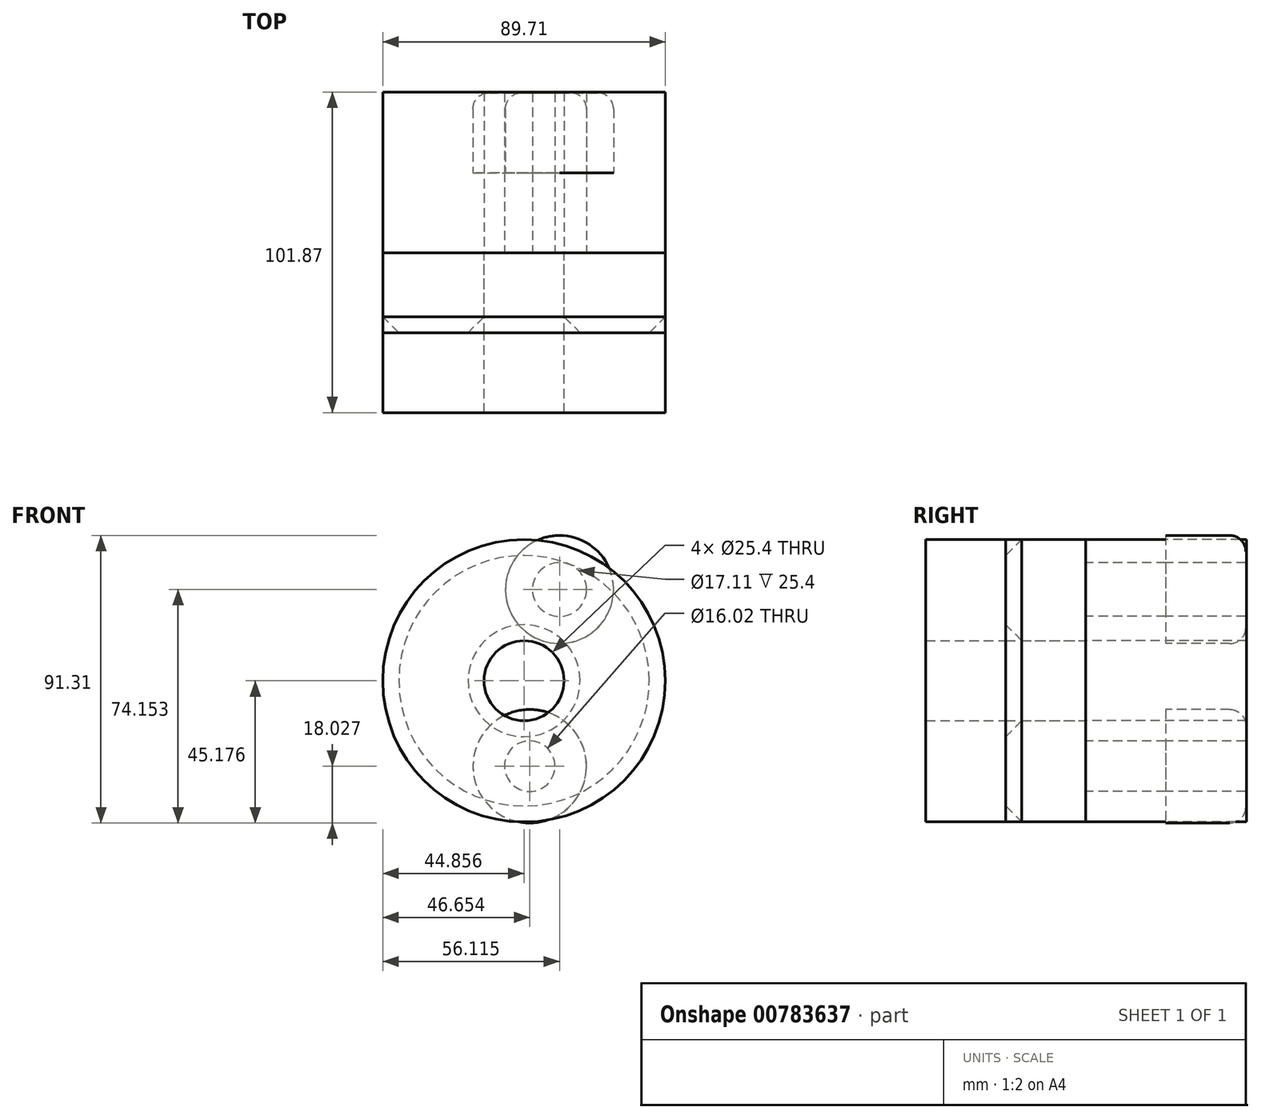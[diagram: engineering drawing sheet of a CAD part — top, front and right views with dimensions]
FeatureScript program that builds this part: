
annotation { "Feature Type Name" : "Feature", "Feature Type Description" : "" }
export const myFeature = defineFeature(function(context is Context, id is Id, definition is map)
    precondition{}
    {
        {
            var Q0;
            Q0=qCreatedBy(makeId("Front.planeOp"),FACE);
            var sketch = newSketch(context, id + "F0", { "sketchPlane" : qUnion([Q0])});
            skCircle(sketch, "E0", {"center": v(-24.07, 18.9) * mm, "radius": 44.86 * mm});
            skSolve(sketch);
        }
        {
            var Q0;
            Q0=makeQuery(id+"F0.imprint","IMPRINT",FACE,{"disambiguationData":[TD([[makeQuery(id+"F0.imprint","IMPRINT",EDGE,{"derivedFrom":sQuery(id+"F0.wireOp",EDGE,"E0")}),1.0]])]});
            var sketch = newSketch(context, id + "F1", { "sketchPlane" : qUnion([Q0])});
            skLineSegment(sketch, "E1.bottom", {"start": v(-31.53, 27.59) * mm, "end": v(-13.5, 27.59) * mm});
            skLineSegment(sketch, "E1.top", {"start": v(-31.53, 11.47) * mm, "end": v(-13.5, 11.47) * mm});
            skLineSegment(sketch, "E1.left", {"start": v(-31.53, 27.59) * mm, "end": v(-31.53, 11.47) * mm});
            skLineSegment(sketch, "E1.right", {"start": v(-13.5, 27.59) * mm, "end": v(-13.5, 11.47) * mm});
            skPoint(sketch, "E1.middle", {"position": v(-22.52, 19.53) * mm});
            skSolve(sketch);
        }
        {
            var Q0;
            Q0=makeQuery(id+"F1.imprint","IMPRINT",FACE,{"disambiguationData":[TD([[makeQuery(id+"F1.imprint","IMPRINT",EDGE,{"derivedFrom":sQuery(id+"F1.wireOp",EDGE,"E1.bottom")}),1.0]])]});
            var Q1;
            Q1=makeQuery(id+"F0.imprint","IMPRINT",FACE,{"disambiguationData":[TD([[makeQuery(id+"F0.imprint","IMPRINT",EDGE,{"derivedFrom":sQuery(id+"F0.wireOp",EDGE,"E0")}),1.0]])]});
            var Q2;
            Q2 = qSketchRegion(id + "F1", true);
            extrude(context, id + "F2", {"entities" : qUnion([Q0, Q1, Q2]), "depth" : 25.4 * mm, "offsetDistance" : 25.4 * mm});
        }
        {
            var Q0;
            {var subQ0=sQuery(id+"F0.wireOp",EDGE,"E0");Q0=makeQuery(id+"F2.opExtrude","CAP_FACE",FACE,{"disambiguationData":[OSD([subQ0]),TDD([makeQuery(id+"F0.imprint","IMPRINT",EDGE,{"derivedFrom":subQ0})])],"isStart":false});}
            var sketch = newSketch(context, id + "F3", { "sketchPlane" : qUnion([Q0])});
            skPoint(sketch, "E2", {"position": v(-24.07, 18.9) * mm});
            skSolve(sketch);
        }
        {
            var Q0;
            {var subQ0=sQuery(id+"F0.wireOp",EDGE,"E0");Q0=makeQuery(id+"F2.opExtrude","CAP_FACE",FACE,{"disambiguationData":[OSD([subQ0]),TDD([makeQuery(id+"F0.imprint","IMPRINT",EDGE,{"derivedFrom":subQ0})])],"isStart":true});}
            var sketch = newSketch(context, id + "F4", { "sketchPlane" : qUnion([Q0])});
            skPoint(sketch, "E3", {"position": v(24.07, 18.9) * mm});
            skSolve(sketch);
        }
        {
            var Q0;
            Q0=sQuery(id+"F4.wireOp",VERTEX,"E3");
            var Q1;
            Q1=sQuery(id+"F3.wireOp",VERTEX,"E2");
            var Q2;
            {var subQ0=sQuery(id+"F0.wireOp",EDGE,"E0");Q2=makeQuery(id+"F2.opExtrude","SWEPT_BODY",BODY,{"disambiguationData":[OSD([subQ0]),TDD([makeQuery(id+"F0.imprint","IMPRINT",EDGE,{"derivedFrom":subQ0})])]});}
            var Q3;
            {var subQ0=sQuery(id+"F0.wireOp",EDGE,"E0");Q3=makeQuery(id+"F2.opExtrude","SWEPT_BODY",BODY,{"disambiguationData":[OSD([subQ0]),TDD([makeQuery(id+"F1.imprint","IMPRINT",EDGE,{"derivedFrom":makeQuery(id+"F0.imprint","IMPRINT",EDGE,{"derivedFrom":subQ0})})])]});}
            hole(context, id + "F5", {"style" : HoleStyle.SIMPLE, "endStyle" : HoleEndStyle.THROUGH, "holeDiameter" : 25.4 * mm, "majorDiameter" : 6.35 * mm, "isTappedThrough" : true, "tappedDepth" : 12.7 * mm, "tapClearance" : 3, "locations" : qUnion([Q0, Q1]), "scope" : qUnion([Q2, Q3])});
        }
        {
            var Q0;
            {var subQ0=sQuery(id+"F0.wireOp",EDGE,"E0");Q0=makeQuery(id+"F2.opExtrude","CAP_FACE",FACE,{"disambiguationData":[OSD([subQ0]),TDD([makeQuery(id+"F1.imprint","IMPRINT",EDGE,{"derivedFrom":makeQuery(id+"F0.imprint","IMPRINT",EDGE,{"derivedFrom":subQ0})})])],"isStart":false});}
            chamfer(context, id + "F6", {"entities" : qUnion([Q0]), "width" : 5.08 * mm, "tangentPropagation" : true});
        }
        {
            var Q0;
            {var subQ0=sQuery(id+"F0.wireOp",EDGE,"E0");Q0=makeQuery(id+"F2.opExtrude","CAP_FACE",FACE,{"disambiguationData":[OSD([subQ0]),TDD([makeQuery(id+"F0.imprint","IMPRINT",EDGE,{"derivedFrom":subQ0})])],"isStart":false});}
            var sketch = newSketch(context, id + "F7", { "sketchPlane" : qUnion([Q0])});
            skSolve(sketch);
        }
        {
            var Q0;
            {var subQ0=sQuery(id+"F0.wireOp",EDGE,"E0");var subQ1=makeQuery(id+"F0.imprint","IMPRINT",EDGE,{"derivedFrom":subQ0});Q0=makeQuery(id+"F7.imprint","IMPRINT",FACE,{"disambiguationData":[TD([[makeQuery(id+"F7.imprint","IMPRINT",EDGE,{"derivedFrom":makeQuery(id+"F2.opExtrude","CAP_EDGE",EDGE,{"disambiguationData":[OSD([subQ0]),TDD([subQ1])],"isStart":false})}),1.0]])]});}
            extrude(context, id + "F8", {"entities" : qUnion([Q0]), "depth" : 25.4 * mm, "offsetDistance" : 25.4 * mm});
        }
        {
            var Q0;
            {var subQ0=sQuery(id+"F0.wireOp",EDGE,"E0");Q0=makeQuery(id+"F2.opExtrude","CAP_FACE",FACE,{"disambiguationData":[OSD([subQ0]),TDD([makeQuery(id+"F1.imprint","IMPRINT",EDGE,{"derivedFrom":makeQuery(id+"F0.imprint","IMPRINT",EDGE,{"derivedFrom":subQ0})})])],"isStart":true});}
            var sketch = newSketch(context, id + "F9", { "sketchPlane" : qUnion([Q0])});
            skCircle(sketch, "E4", {"center": v(12.81, 47.88) * mm, "radius": 8.56 * mm});
            skSolve(sketch);
        }
        {
            var Q0;
            Q0 = qSketchRegion(id + "F9", true);
            var Q1;
            Q1=makeQuery(id+"F9.imprint","IMPRINT",FACE,{"disambiguationData":[TD([[makeQuery(id+"F9.imprint","IMPRINT",EDGE,{"derivedFrom":sQuery(id+"F9.wireOp",EDGE,"E4")}),1.0]])]});
            extrude(context, id + "F10", {"entities" : qUnion([Q0, Q1]), "depth" : 25.4 * mm, "offsetDistance" : 25.4 * mm});
        }
        {
            var Q0;
            {var subQ0=sQuery(id+"F0.wireOp",EDGE,"E0");Q0=makeQuery(id+"F2.opExtrude","CAP_FACE",FACE,{"disambiguationData":[OSD([subQ0]),TDD([makeQuery(id+"F1.imprint","IMPRINT",EDGE,{"derivedFrom":makeQuery(id+"F0.imprint","IMPRINT",EDGE,{"derivedFrom":subQ0})})])],"isStart":true});}
            var sketch = newSketch(context, id + "F11", { "sketchPlane" : qUnion([Q0])});
            skCircle(sketch, "E5", {"center": v(22.28, -8.24) * mm, "radius": 8 * mm});
            skSolve(sketch);
        }
        {
            var Q0;
            Q0=makeQuery(id+"F11.imprint","IMPRINT",FACE,{"disambiguationData":[TD([[makeQuery(id+"F11.imprint","IMPRINT",EDGE,{"derivedFrom":sQuery(id+"F11.wireOp",EDGE,"E5")}),1.0]])]});
            var Q1;
            Q1 = qSketchRegion(id + "F11", true);
            extrude(context, id + "F12", {"entities" : qUnion([Q0, Q1]), "depth" : 25.4 * mm, "offsetDistance" : 25.4 * mm});
        }
        {
            var Q0;
            Q0=makeQuery(id+"F12.opExtrude","CAP_FACE",FACE,{"disambiguationData":[OSD([sQuery(id+"F11.wireOp",EDGE,"E5")])],"isStart":false});
            var sketch = newSketch(context, id + "F13", { "sketchPlane" : qUnion([Q0])});
            skCircle(sketch, "E6", {"center": v(22.28, -8.24) * mm, "radius": 18.02 * mm});
            skSolve(sketch);
        }
        {
            var Q0;
            Q0=makeQuery(id+"F13.imprint","IMPRINT",FACE,{"disambiguationData":[TD([[makeQuery(id+"F13.imprint","IMPRINT",EDGE,{"derivedFrom":sQuery(id+"F13.wireOp",EDGE,"E6")}),1.0]])]});
            extrude(context, id + "F14", {"entities" : qUnion([Q0]), "depth" : 25.4 * mm, "offsetDistance" : 25.4 * mm});
        }
        {
            var Q0;
            Q0=makeQuery(id+"F10.opExtrude","CAP_FACE",FACE,{"disambiguationData":[OSD([sQuery(id+"F9.wireOp",EDGE,"E4")])],"isStart":false});
            var sketch = newSketch(context, id + "F15", { "sketchPlane" : qUnion([Q0])});
            skCircle(sketch, "E7", {"center": v(12.81, 47.88) * mm, "radius": 17.16 * mm});
            skSolve(sketch);
        }
        {
            var Q0;
            Q0=makeQuery(id+"F15.imprint","IMPRINT",FACE,{"disambiguationData":[TD([[makeQuery(id+"F15.imprint","IMPRINT",EDGE,{"derivedFrom":sQuery(id+"F15.wireOp",EDGE,"E7")}),1.0]])]});
            extrude(context, id + "F16", {"entities" : qUnion([Q0]), "depth" : 25.4 * mm, "offsetDistance" : 25.4 * mm});
        }
        {
            var Q0;
            Q0=makeQuery(id+"F14.opExtrude","CAP_EDGE",EDGE,{"disambiguationData":[OSD([sQuery(id+"F13.wireOp",EDGE,"E6")])],"isStart":false});
            fillet(context, id + "F17", {"entities" : qUnion([Q0]), "radius" : 5.08 * mm, "tangentPropagation" : true, "allowEdgeOverflow" : false});
        }
        {
            var Q0;
            Q0=makeQuery(id+"F16.opExtrude","CAP_EDGE",EDGE,{"disambiguationData":[OSD([sQuery(id+"F15.wireOp",EDGE,"E7")])],"isStart":false});
            fillet(context, id + "F18", {"entities" : qUnion([Q0]), "radius" : 5.08 * mm, "tangentPropagation" : true, "allowEdgeOverflow" : false});
        }
        {
            var Q0;
            {var subQ0=sQuery(id+"F0.wireOp",EDGE,"E0");Q0=makeQuery(id+"F2.opExtrude","CAP_FACE",FACE,{"disambiguationData":[OSD([subQ0]),TDD([makeQuery(id+"F1.imprint","IMPRINT",EDGE,{"derivedFrom":makeQuery(id+"F0.imprint","IMPRINT",EDGE,{"derivedFrom":subQ0})})])],"isStart":true});}
            var sketch = newSketch(context, id + "F19", { "sketchPlane" : qUnion([Q0])});
            skCircle(sketch, "E8", {"center": v(24.07, 18.9) * mm, "radius": 44.83 * mm});
            skSolve(sketch);
        }
        {
            var Q0;
            Q0=makeQuery(id+"F19.imprint","IMPRINT",FACE,{"disambiguationData":[TD([[makeQuery(id+"F19.imprint","IMPRINT",EDGE,{"derivedFrom":sQuery(id+"F19.wireOp",EDGE,"E8")}),1.0]])]});
            extrude(context, id + "F20", {"entities" : qUnion([Q0]), "depth" : 51.07 * mm, "offsetDistance" : 25.4 * mm});
        }
    });
